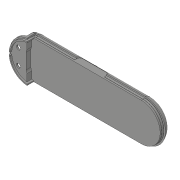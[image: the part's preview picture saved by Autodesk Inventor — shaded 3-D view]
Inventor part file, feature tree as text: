
AUTODESK INVENTOR PART (.ipt)
format: ipt  version: 2019.4 (Build 234330000, 330)  size: 342,528 bytes
history: native  units: mm
features: hole x3, sketch x3, other x1, chamfer x1, imported_body x1
ambient origin geometry x8: Origin, YZ Plane, XZ Plane, XY Plane, X Axis, Y Axis, Z Axis, Center Point
bodies: Body1 (feature_tree)
feature tree (9):
  other  "ソリッド1"
  hole  "穴1"  [1 undecoded]
  hole  "穴2"  [1 undecoded]
  hole  "穴3"  [1 undecoded]
  chamfer  "面取り1"  [1 undecoded]
  sketch  "スケッチ4"
  sketch  "スケッチ5"
  sketch  "スケッチ7"
  imported_body  "Base1"
note: 4 required parameter values undecoded (feature->parameter linkage not recoverable at this tier; creation-order binding heuristic only, values carry confidence <= 0.55)
